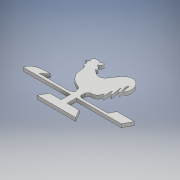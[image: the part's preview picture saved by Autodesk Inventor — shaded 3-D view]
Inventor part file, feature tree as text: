
AUTODESK INVENTOR PART (.ipt)
format: ipt  version: 2017.1 (Build 211199000, 199)  size: 172,544 bytes
history: native  units: mm
features: other x1, extrude x1, sketch x1
ambient origin geometry x8: Origin, YZ Plane, XZ Plane, XY Plane, X Axis, Y Axis, Z Axis, Center Point
bodies: Body1 (feature_tree)
feature tree (3):
  other  "ソリッド1"
  extrude  "押し出し1"  Depth=4.0mm TaperAngle=0.0deg
  sketch  "スケッチ1"
